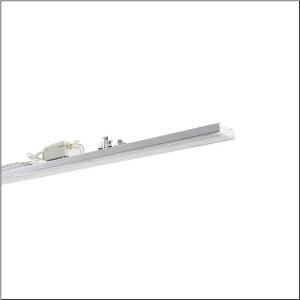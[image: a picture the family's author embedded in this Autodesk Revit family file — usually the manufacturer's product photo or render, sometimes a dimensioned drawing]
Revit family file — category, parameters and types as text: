
# Revit family: licross_11_recessed_ho_51te12mn4exm
name_source: partatom
category: Lighting Fixtures
units: mm (PartAtom-declared; Revit-internal decimal feet)

## family parameters
Cut with Voids When Loaded = No
Host = Face
Light Source = No
Part Type = Normal
Room Calculation Point = No
Round Connector Dimension = Use Diameter
Shared = No

## types (1)
- --- (1 x LED, 14100 lm, 74.5 W, 4000K)
    Apparent Load = 75 VA
    CIE Flux Codes = 66 91 98 100 100
    Color Rendering = 80
    Color Temperature = 4000K
    Default Elevation = 1800 mm
    Description = Licross 11 Recessed HO, luminaire insert, of sheet steel, galvanised, coil coated, white, length: 1.500mm, width: 66mm, height: 67mm, LED rated luminous flux: 14.100lm, light colour: 840, SDCM (Standard Deviation of Colour Matching)MacAdam ≤ 2 SDCM (initial), control gear: ON/OFF Multilumen, with plug, 3-pole, with phase selection, mains connection: 220..240V, AC, 50/60Hz, rated input power: 75W, internal wiring halogen-free, primary optical cover: cover, of PMMA, light emission: direct distribution, primary light characteristic: symmetric, protection rating (complete): IP54, insulation class (complete): insulation class I (protective earthing), certification: CE, ENEC, VDE, UKCA, protection symbol: D if used in an environment with non-conductive dust loads with corresponding accessories, impact resistance: IK06, permissible ambient temperature for indoor applications: -35..+35°C, corresponds to IFS (International Featured Standards) requirements for safety and quality in the food industry, reducing of maximum allowable ambient temperature of 5°C with ceiling mounting, The light source and the operating device comply with the requirements of the Ecodesign Regulation (EU) 2019/2020 and are replaceable in accordance with this regulation, packaging unit: 1 piece
    Height = 58 mm
    Lamp = 1 x LED
    Lamp Light Flux = 14100 lm
    Lamp Power = 74.5 W
    Lamp count = 1
    Length = 1500 mm
    Luminous efficacy = 189 lm/W
    Manufacturer = Siteco
    ModVariant = No
    Model = 51TE12MN4EXM
    Mounting Place = Ceiling
    Mounting Type = Pendant
    Number of Poles = 1
    OnlyDefault = Yes
    Power Factor = 1
    Product Name = Licross 11 Recessed HO
    Product group = luminaire insert | ceiling pendant
    ProductGroupID = 901
    Protection Class = Protection class I
    Protection Degree = IP 54
    RLX_Detail_Level = 1
    RLX_Emergency_Light_Flux = 0 lm
    RLX_Emergency_Type = 0
    RLX_Emergency_Type_DB = No
    RlxData = <blob elided: 22461 chars, md5=94b71926>
    Socket = socket
    Standby Power = 0 W
    System Light Flux = 14100 lm
    System Power = 75 W
    Type Comments = factory setting: luminous flux: 100 % | (A | C | E) | 174 mA
    Type Image = l_1296930.jpg
    URL = http://relux.com
    VarID = @adj_091467
    Voltage = 0 V
    Weight = 0.00 kg
    Width = 66 mm

## geometry (parser evidence)
native form markers: Blend x4, Sweep x11
no freeform markers — native parametric forms only
